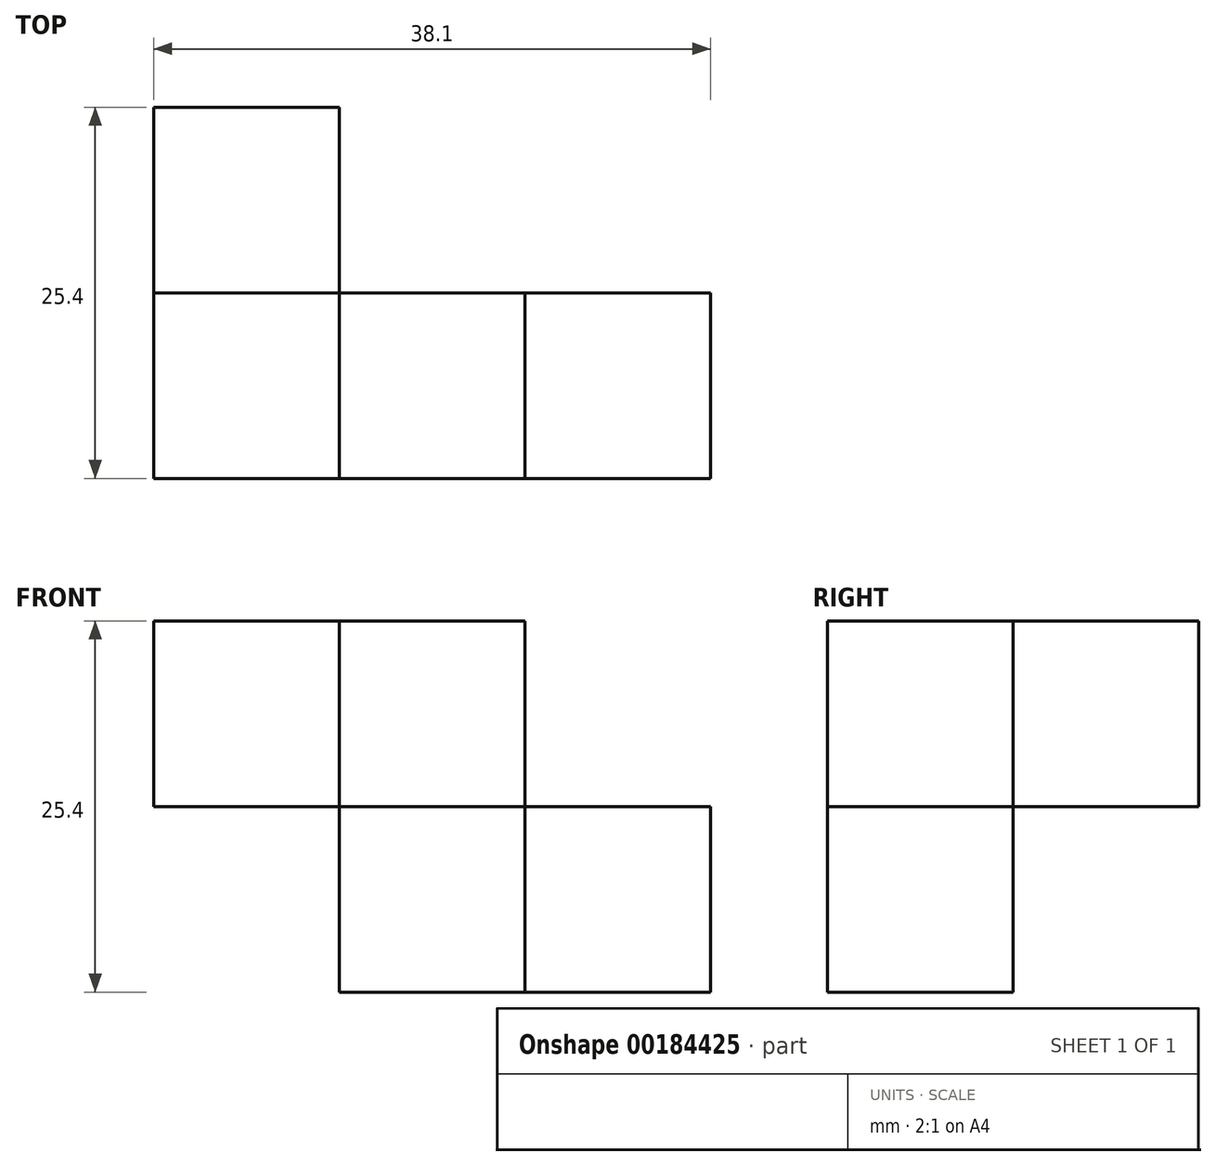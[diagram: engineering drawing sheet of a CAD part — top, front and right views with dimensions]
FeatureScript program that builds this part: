
annotation { "Feature Type Name" : "Feature", "Feature Type Description" : "" }
export const myFeature = defineFeature(function(context is Context, id is Id, definition is map)
    precondition{}
    {
        {
            var Q0;
            Q0=qCreatedBy(makeId("Front.planeOp"),FACE);
            var sketch = newSketch(context, id + "F0", { "sketchPlane" : qUnion([Q0])});
            skLineSegment(sketch, "E0.bottom", {"start": v(95.17, 3.02) * mm, "end": v(107.87, 3.02) * mm});
            skLineSegment(sketch, "E0.top", {"start": v(95.17, -9.68) * mm, "end": v(107.87, -9.68) * mm});
            skLineSegment(sketch, "E0.left", {"start": v(95.17, 3.02) * mm, "end": v(95.17, -9.68) * mm});
            skLineSegment(sketch, "E0.right", {"start": v(107.87, 3.02) * mm, "end": v(107.87, -9.68) * mm});
            skSolve(sketch);
        }
        {
            var Q0;
            Q0 = qSketchRegion(id + "F0", true);
            extrude(context, id + "F1", {"entities" : qUnion([Q0]), "depth" : 12.7 * mm});
        }
        {
            var Q0;
            Q0=makeQuery(id+"F1.opExtrude","SWEPT_BODY",BODY,{"disambiguationData":[OSD([sQuery(id+"F0.wireOp",EDGE,"E0.bottom"),sQuery(id+"F0.wireOp",EDGE,"E0.top"),sQuery(id+"F0.wireOp",EDGE,"E0.left"),sQuery(id+"F0.wireOp",EDGE,"E0.right")])]});
            var Q1;
            Q1=makeQuery(id+"F1.opExtrude","CAP_EDGE",EDGE,{"disambiguationData":[OSD([sQuery(id+"F0.wireOp",EDGE,"E0.bottom")])],"isStart":false});
            transform(context, id + "F2", {"entities" : qUnion([Q0]), "transformType" : TransformType.TRANSLATION_ENTITY, "oppositeDirectionEntity" : false, "transformLine" : qUnion([Q1]), "makeCopy" : true});
        }
        {
            var Q0;
            Q0=makeQuery(id+"F1.opExtrude","SWEPT_BODY",BODY,{"disambiguationData":[OSD([sQuery(id+"F0.wireOp",EDGE,"E0.bottom"),sQuery(id+"F0.wireOp",EDGE,"E0.top"),sQuery(id+"F0.wireOp",EDGE,"E0.left"),sQuery(id+"F0.wireOp",EDGE,"E0.right")])]});
            transform(context, id + "F3", {"entities" : qUnion([Q0]), "transformType" : TransformType.TRANSLATION_3D, "dx" : 0 * mm, "dy" : 0 * mm, "dz" : 12.7 * mm, "makeCopy" : true});
        }
        {
            var Q0;
            Q0=makeQuery(id+"F3.opPattern","COPY",EDGE,{"derivedFrom":makeQuery(id+"F1.opExtrude","SWEPT_EDGE",EDGE,{"disambiguationData":[OSD([sQuery(id+"F0.wireOp",EDGE,"E0.bottom"),sQuery(id+"F0.wireOp",EDGE,"E0.right")])]}),"instanceName":"1"});
            cPoint(context, id + "F4", {"entities" : qUnion([Q0]), "parameter" : 0.5});
        }
        {
            var Q0;
            Q0=makeQuery(id+"F3.opPattern","COPY",EDGE,{"derivedFrom":makeQuery(id+"F1.opExtrude","SWEPT_EDGE",EDGE,{"disambiguationData":[OSD([sQuery(id+"F0.wireOp",EDGE,"E0.bottom"),sQuery(id+"F0.wireOp",EDGE,"E0.left")])]}),"instanceName":"1"});
            cPoint(context, id + "F5", {"entities" : qUnion([Q0]), "parameter" : 0.5});
        }
        {
            var Q0;
            Q0=makeQuery(id+"F3.opPattern","COPY",BODY,{"derivedFrom":makeQuery(id+"F1.opExtrude","SWEPT_BODY",BODY,{"disambiguationData":[OSD([sQuery(id+"F0.wireOp",EDGE,"E0.bottom"),sQuery(id+"F0.wireOp",EDGE,"E0.top"),sQuery(id+"F0.wireOp",EDGE,"E0.left"),sQuery(id+"F0.wireOp",EDGE,"E0.right")])]}),"instanceName":"1"});
            var Q1;
            Q1 = qCreatedBy(id + "F4" ,VERTEX);
            var Q2;
            Q2 = qCreatedBy(id + "F5" ,VERTEX);
            transform(context, id + "F6", {"entities" : qUnion([Q0]), "transformType" : TransformType.TRANSLATION_ENTITY, "oppositeDirectionEntity" : false, "transformLine" : qUnion([Q1, Q2]), "makeCopy" : true});
        }
        {
            var Q0;
            Q0=makeQuery(id+"F6.opPattern","COPY",EDGE,{"derivedFrom":makeQuery(id+"F3.opPattern","COPY",EDGE,{"derivedFrom":makeQuery(id+"F1.opExtrude","CAP_EDGE",EDGE,{"disambiguationData":[OSD([sQuery(id+"F0.wireOp",EDGE,"E0.bottom")])],"isStart":false}),"instanceName":"1"}),"instanceName":"1"});
            cPoint(context, id + "F7", {"entities" : qUnion([Q0]), "parameter" : 0.5});
        }
        {
            var Q0;
            Q0=makeQuery(id+"F6.opPattern","COPY",EDGE,{"derivedFrom":makeQuery(id+"F3.opPattern","COPY",EDGE,{"derivedFrom":makeQuery(id+"F1.opExtrude","CAP_EDGE",EDGE,{"disambiguationData":[OSD([sQuery(id+"F0.wireOp",EDGE,"E0.bottom")])],"isStart":true}),"instanceName":"1"}),"instanceName":"1"});
            cPoint(context, id + "F8", {"entities" : qUnion([Q0]), "parameter" : 0.5});
        }
        {
            var Q0;
            Q0=makeQuery(id+"F6.opPattern","COPY",BODY,{"derivedFrom":makeQuery(id+"F3.opPattern","COPY",BODY,{"derivedFrom":makeQuery(id+"F1.opExtrude","SWEPT_BODY",BODY,{"disambiguationData":[OSD([sQuery(id+"F0.wireOp",EDGE,"E0.bottom"),sQuery(id+"F0.wireOp",EDGE,"E0.top"),sQuery(id+"F0.wireOp",EDGE,"E0.left"),sQuery(id+"F0.wireOp",EDGE,"E0.right")])]}),"instanceName":"1"}),"instanceName":"1"});
            var Q1;
            Q1 = qCreatedBy(id + "F7" ,VERTEX);
            var Q2;
            Q2 = qCreatedBy(id + "F8" ,VERTEX);
            transform(context, id + "F9", {"entities" : qUnion([Q0]), "transformType" : TransformType.TRANSLATION_ENTITY, "oppositeDirectionEntity" : false, "transformLine" : qUnion([Q1, Q2]), "makeCopy" : true});
        }
    });
